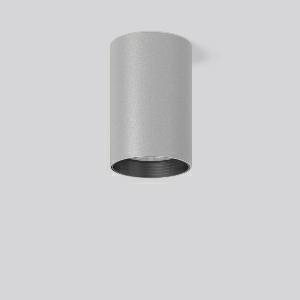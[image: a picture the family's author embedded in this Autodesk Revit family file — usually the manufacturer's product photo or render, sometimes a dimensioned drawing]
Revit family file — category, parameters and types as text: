
# Revit family: heledon_maxi_a_931242_004_76_1c00
name_source: partatom
category: Lighting Fixtures
units: mm (PartAtom-declared; Revit-internal decimal feet)

## family parameters
Cut with Voids When Loaded = No
Host = Face
Light Source = No
Part Type = Normal
Room Calculation Point = No
Round Connector Dimension = Use Diameter
Shared = No

## types (1)
- HELEDON maxi A (1 x LED Modul 920 meat+, 1850 lm, 2000)
    Apparent Load = 33 VA
    Approval mark = CE
    CIE Flux Codes = 96 99 100 100 100
    Color Rendering = 90
    Color Temperature = 2000
    Default Elevation = 1800 mm
    Description = Series: HELEDON maxi
Cylindrical surface-mounted downlight. Housing: die-cast aluminium, powder-coated. Internal ceiling frame polycarbonate with bayonet mounting. Black plastic ring and recessed LED to prevent glare from the side. Optical assembly with lens made of plastic (polycarbonate) for the best homogeneous light distribution - can be changed without tools. Special LED for illumination of meat included. Suitable for Ceiling mounting. Easy installation with a separate ceiling frame with bayonet mounting and plug connection. Driver integrated. Connected via plug-in connector. High quality converter without flickering and stroboscopic effect. The following accessories can be mounted without use of tools: interchangeable lenses, decorative glasses, honeycomb louvre, clear and frosted diffusers, white interchangeable plastic ring. 
Colour: silver
Diameter: 123 mm
Height: 183 mm
Lamp: LED
Socket: without socket
Colour temperature: meat +
System power: 33 W
Rated luminous flux: 1850 lm
Luminous efficiency: 56 lm/W
Control gear: Converter, dimmable, DALI
Protection class: I
Type of protection: IP 20
    Height = 183 mm
    Lamp = 1 x LED Modul 920 meat+
    Lamp Light Flux = 1850 lm
    Lamp count = 1
    Length = 123 mm
    Lifetime = 50000 h
    Luminous efficacy = 56 lm/W
    Manufacturer = RZB
    ModVariant = No
    Model = 931242.004.76
    Mounting Place = Ceiling
    Mounting Type = Surface mounted
    Number of Poles = 1
    OnlyDefault = Yes
    Power Factor = 1
    Product Name = HELEDON maxi A
    Product group = Surface mounted downlights
    ProductGroupID = 302
    Protection Class = Protection class I
    Protection Degree = IP 20
    RLX_Detail_Level = 1
    RLX_Emergency_Light_Flux = 0 lm
    RLX_Emergency_Type = 0
    RLX_Emergency_Type_DB = No
    RlxData = <blob elided: 99201 chars, md5=fea175aa>
    Socket = socket
    Standby Power = 0 W
    System Light Flux = 1850 lm
    System Power = 33 W
    Type Comments = Product without accessories
    Type Image = 931193.004.jpg
    URL = http://relux.com
    VarID = ---
    Voltage = 230 V
    Voltage Range = 220-240 V
    Weight = 0.00 kg
    Width = 0 mm  [stored 0 ft]

note: [stored X ft] marks values corroborated as IEEE doubles in the binary element streams (Revit-internal decimal feet)

## geometry (parser evidence)
native form markers: Blend x4, Sweep x8
no freeform markers — native parametric forms only
